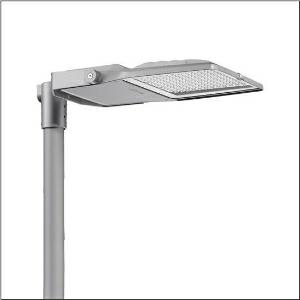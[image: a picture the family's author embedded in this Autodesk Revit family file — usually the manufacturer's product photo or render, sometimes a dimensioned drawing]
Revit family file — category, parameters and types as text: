
# Revit family: floodlight_fl_21_midi___pl64_5xa7782e4e3a_4760
name_source: partatom
category: Lighting Fixtures
units: mm (PartAtom-declared; Revit-internal decimal feet)

## family parameters
Cut with Voids When Loaded = No
Host = Face
Light Source = No
Part Type = Normal
Room Calculation Point = No
Round Connector Dimension = Use Diameter
Shared = No

## types (1)
- --- (1 x LED, 27050 lm, 208.1 W, 4000K)
    Apparent Load = 208 VA
    CIE Flux Codes = 28 80 98 100 100
    Color Rendering = 70
    Color Temperature = 4000K
    Default Elevation = 1800 mm
    Description = Floodlight FL 21 midi, floodlight, primary light control with lens, of PMMA, primary optical cover: protective disc, of toughened safety glass, transparent, light distribution: PL64, light emission: direct distribution, installation type: surface-mounted, LED, High Power LED, rated luminous flux: 27.050lm, luminous efficacy: 129lm/W, light colour: 740, colour temperature: 4000K, control gear: ECG iQ, control: optimised constant luminous flux control (CLO 2.0), Desk-Remote (wireless, voltage-free reading and setting of iQ features in the workshop via application-optimized NFC function/RFID function), Smart-Wire, Night-Set, Temp-Guard, Auto-Match, Street-Remote, with terminal, 6-pole, mains connection: 220..240V, AC, 50/60Hz, start of lifetime: 208W, end of lifetime: 227W, reduction: 90W, luminaire housing, of diecast aluminium, powder-coated, Siteco® metallic grey (DB 702S), corrosivity category C5 according to DIN EN ISO 12944, mast bracket, of steel, galvanised, powder-coated, Siteco® metallic grey (DB 702S), protection rating (complete): IP66, insulation class (complete): insulation class II (safety insulation), certification: CE, protection symbol: D, impact resistance: IK08, permissible operating ambient temperature: -40..+40°C, permissible operating ambient temperature for outdoor applications: -40..+50°C, standard: DIN EN 12944, packaging unit: 1 piece

Light Distribution: PL64
    Height = 76 mm
    Lamp = 1 x LED
    Lamp Light Flux = 27050 lm
    Lamp Power = 208.1 W
    Lamp count = 1
    Length = 657 mm
    Luminous efficacy = 130 lm/W
    Manufacturer = Siteco
    ModVariant = No
    Model = 5XA7782E4E3A
    Number of Poles = 1
    OnlyDefault = Yes
    Power Factor = 1
    Product Name = Floodlight FL 21 midi | PL64
    Product group = floodlight | pylon top
    ProductGroupID = 6101
    Protection Class = Protection class II
    Protection Degree = IP 66
    RLX_Detail_Level = 1
    RlxData = <blob elided: 153257 chars, md5=0d36f391>
    Socket = socket
    Standby Power = 0 W
    System Light Flux = 27050 lm
    System Power = 208 W
    Type Comments = factory setting: luminous flux: 100 % | dim-lin: 254 | 710 mA
    Type Image = l_1007123.jpg
    URL = http://relux.com
    VarID = @adj_015461
    Voltage = 0 V
    Weight = 0.00 kg
    Width = 442 mm

## geometry (parser evidence)
native form markers: Blend x4, Sweep x12
no freeform markers — native parametric forms only
